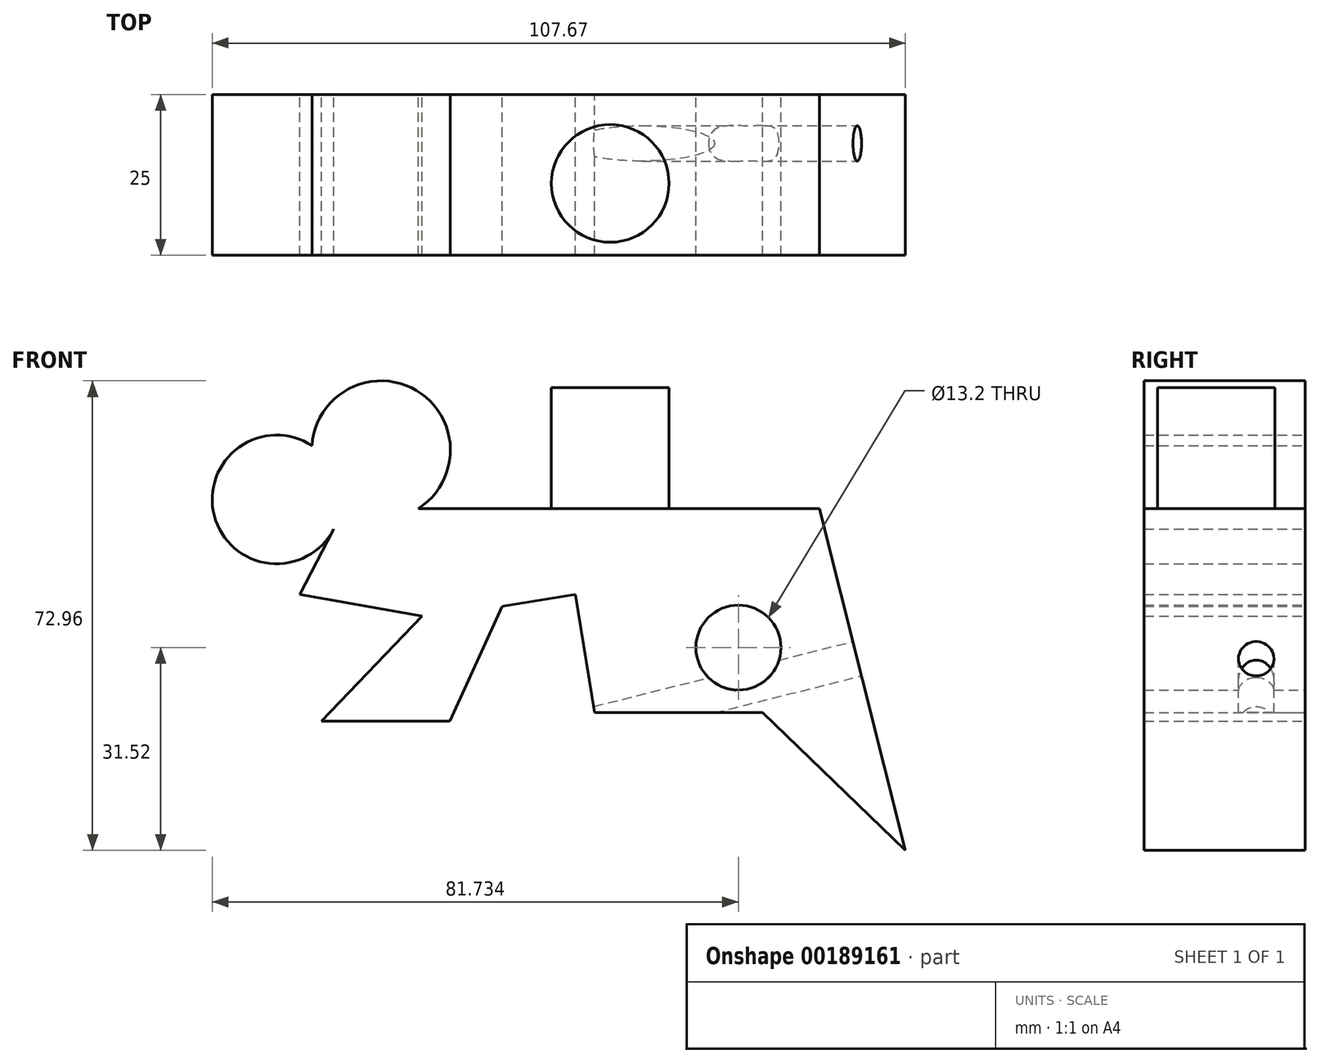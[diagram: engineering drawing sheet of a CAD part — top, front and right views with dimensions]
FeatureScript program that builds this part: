
annotation { "Feature Type Name" : "Feature", "Feature Type Description" : "" }
export const myFeature = defineFeature(function(context is Context, id is Id, definition is map)
    precondition{}
    {
        {
            var Q0;
            Q0=qCreatedBy(makeId("Front.planeOp"),FACE);
            var sketch = newSketch(context, id + "F0", { "sketchPlane" : qUnion([Q0])});
            skLineSegment(sketch, "E0", {"start": v(-41.86, 41.58) * mm, "end": v(20.46, 41.58) * mm});
            skLineSegment(sketch, "E1", {"start": v(20.46, 41.58) * mm, "end": v(33.8, -11.54) * mm});
            skLineSegment(sketch, "E2", {"start": v(33.8, -11.54) * mm, "end": v(11.64, 9.86) * mm});
            skLineSegment(sketch, "E3", {"start": v(11.64, 9.86) * mm, "end": v(-14.45, 9.86) * mm});
            skLineSegment(sketch, "E4", {"start": v(-14.45, 9.86) * mm, "end": v(-17.46, 28.25) * mm});
            skLineSegment(sketch, "E5", {"start": v(-17.46, 28.25) * mm, "end": v(-28.85, 26.4) * mm});
            skLineSegment(sketch, "E6", {"start": v(-28.85, 26.4) * mm, "end": v(-36.98, 8.54) * mm});
            skLineSegment(sketch, "E7", {"start": v(-36.98, 8.54) * mm, "end": v(-56.88, 8.54) * mm});
            skLineSegment(sketch, "E8", {"start": v(-56.88, 8.54) * mm, "end": v(-41.3, 24.87) * mm});
            skLineSegment(sketch, "E9", {"start": v(-41.3, 24.87) * mm, "end": v(-60.26, 28.25) * mm});
            skLineSegment(sketch, "E10", {"start": v(-60.26, 28.25) * mm, "end": v(-55, 38.39) * mm});
            skArc(sketch, "E11", {"start": v(-58.38, 51.34) * mm, "mid": v(-73.55, 40.47) * mm, "end": v(-55, 38.39) * mm});
            skArc(sketch, "E12", {"start": v(-41.86, 41.58) * mm, "mid": v(-42.17, 59.92) * mm, "end": v(-58.38, 51.34) * mm});
            skSolve(sketch);
        }
        {
            var Q0;
            Q0 = qSketchRegion(id + "F0", true);
            extrude(context, id + "F1", {"entities" : qUnion([Q0]), "depth" : 25 * mm});
        }
        {
            var Q0;
            Q0=makeQuery(id+"F1.opExtrude","SWEPT_FACE",FACE,{"disambiguationData":[OSD([sQuery(id+"F0.wireOp",EDGE,"E0")])]});
            var sketch = newSketch(context, id + "F2", { "sketchPlane" : qUnion([Q0])});
            skCircle(sketch, "E13", {"center": v(-12.05, -13.83) * mm, "radius": 9.14 * mm});
            skSolve(sketch);
        }
        {
            var Q0;
            Q0=makeQuery(id+"F2.imprint","IMPRINT",FACE,{"disambiguationData":[TD([[makeQuery(id+"F2.imprint","IMPRINT",EDGE,{"derivedFrom":sQuery(id+"F2.wireOp",EDGE,"E13")}),1.0]])]});
            extrude(context, id + "F3", {"entities" : qUnion([Q0]), "operationType" : NewBodyOperationType.ADD, "depth" : 18.8 * mm});
        }
        {
            var Q0;
            Q0=makeQuery(id+"F1.opExtrude","SWEPT_FACE",FACE,{"disambiguationData":[OSD([sQuery(id+"F0.wireOp",EDGE,"E1")])]});
            var sketch = newSketch(context, id + "F4", { "sketchPlane" : qUnion([Q0])});
            skCircle(sketch, "E14", {"center": v(-10.5, 14.37) * mm, "radius": 2.78 * mm});
            skSolve(sketch);
        }
        {
            var Q0;
            Q0=makeQuery(id+"F4.imprint","IMPRINT",FACE,{"disambiguationData":[TD([[makeQuery(id+"F4.imprint","IMPRINT",EDGE,{"derivedFrom":sQuery(id+"F4.wireOp",EDGE,"E14")}),-1.0]])]});
            var sketch = newSketch(context, id + "F5", { "sketchPlane" : qUnion([Q0])});
            skLineSegment(sketch, "E15", {"start": v(0, 11.67) * mm, "end": v(-25.24, 10.44) * mm});
            skLineSegment(sketch, "E16", {"start": v(-25.24, 10.44) * mm, "end": v(-12.9, 35.12) * mm});
            skLineSegment(sketch, "E17", {"start": v(-12.9, 35.12) * mm, "end": v(-7.6, 11.3) * mm});
            skLineSegment(sketch, "E18", {"start": v(-7.6, 11.3) * mm, "end": v(0, -10.03) * mm});
            skLineSegment(sketch, "E19", {"start": v(0, -10.03) * mm, "end": v(-25.24, 10.44) * mm});
            skSolve(sketch);
        }
        {
            var Q0;
            Q0=sQuery(id+"F5.wireOp",VERTEX,"E18.start");
            var Q1;
            Q1=makeQuery(id+"F1.opExtrude","SWEPT_BODY",BODY,{"disambiguationData":[OSD([sQuery(id+"F0.wireOp",EDGE,"E0"),sQuery(id+"F0.wireOp",EDGE,"E1"),sQuery(id+"F0.wireOp",EDGE,"E2"),sQuery(id+"F0.wireOp",EDGE,"E3"),sQuery(id+"F0.wireOp",EDGE,"E4"),sQuery(id+"F0.wireOp",EDGE,"E5"),sQuery(id+"F0.wireOp",EDGE,"E6"),sQuery(id+"F0.wireOp",EDGE,"E7"),sQuery(id+"F0.wireOp",EDGE,"E8"),sQuery(id+"F0.wireOp",EDGE,"E9"),sQuery(id+"F0.wireOp",EDGE,"E10"),sQuery(id+"F0.wireOp",EDGE,"E11"),sQuery(id+"F0.wireOp",EDGE,"E12")])]});
            hole(context, id + "F6", {"style" : HoleStyle.SIMPLE, "endStyle" : HoleEndStyle.THROUGH, "holeDiameter" : 5.5 * mm, "locations" : qUnion([Q0]), "scope" : qUnion([Q1]), "isTappedThrough" : true});
        }
        {
            var Q0;
            Q0=makeQuery(id+"F1.opExtrude","CAP_FACE",FACE,{"disambiguationData":[OSD([sQuery(id+"F0.wireOp",EDGE,"E0"),sQuery(id+"F0.wireOp",EDGE,"E1"),sQuery(id+"F0.wireOp",EDGE,"E2"),sQuery(id+"F0.wireOp",EDGE,"E3"),sQuery(id+"F0.wireOp",EDGE,"E4"),sQuery(id+"F0.wireOp",EDGE,"E5"),sQuery(id+"F0.wireOp",EDGE,"E6"),sQuery(id+"F0.wireOp",EDGE,"E7"),sQuery(id+"F0.wireOp",EDGE,"E8"),sQuery(id+"F0.wireOp",EDGE,"E9"),sQuery(id+"F0.wireOp",EDGE,"E10"),sQuery(id+"F0.wireOp",EDGE,"E11"),sQuery(id+"F0.wireOp",EDGE,"E12")])],"isStart":true});
            var sketch = newSketch(context, id + "F7", { "sketchPlane" : qUnion([Q0])});
            skLineSegment(sketch, "E20", {"start": v(-1.53, 41.58) * mm, "end": v(-3.3, 9.86) * mm});
            skLineSegment(sketch, "E21", {"start": v(-24.39, 25.93) * mm, "end": v(16.36, 21.5) * mm});
            skSolve(sketch);
        }
        {
            var Q0;
            {var subQ0=makeQuery(id+"F1.opExtrude","CAP_EDGE",EDGE,{"disambiguationData":[OSD([sQuery(id+"F0.wireOp",EDGE,"E2")])],"isStart":true});Q0=makeQuery(id+"F7.imprint","IMPRINT",FACE,{"disambiguationData":[TD([[makeQuery(id+"F7.imprint","IMPRINT",EDGE,{"derivedFrom":subQ0}),1.0]])]});}
            var sketch = newSketch(context, id + "F8", { "sketchPlane" : qUnion([Q0])});
            skCircle(sketch, "E22", {"center": v(-7.85, 19.98) * mm, "radius": 3.6 * mm});
            skSolve(sketch);
        }
        {
            var Q0;
            Q0=sQuery(id+"F8.wireOp",VERTEX,"E22.center");
            var Q1;
            Q1=makeQuery(id+"F1.opExtrude","SWEPT_BODY",BODY,{"disambiguationData":[OSD([sQuery(id+"F0.wireOp",EDGE,"E0"),sQuery(id+"F0.wireOp",EDGE,"E1"),sQuery(id+"F0.wireOp",EDGE,"E2"),sQuery(id+"F0.wireOp",EDGE,"E3"),sQuery(id+"F0.wireOp",EDGE,"E4"),sQuery(id+"F0.wireOp",EDGE,"E5"),sQuery(id+"F0.wireOp",EDGE,"E6"),sQuery(id+"F0.wireOp",EDGE,"E7"),sQuery(id+"F0.wireOp",EDGE,"E8"),sQuery(id+"F0.wireOp",EDGE,"E9"),sQuery(id+"F0.wireOp",EDGE,"E10"),sQuery(id+"F0.wireOp",EDGE,"E11"),sQuery(id+"F0.wireOp",EDGE,"E12")])]});
            hole(context, id + "F9", {"style" : HoleStyle.SIMPLE, "endStyle" : HoleEndStyle.THROUGH, "standardTappedOrClearance" : lookupTablePath({ "standard" : "ISO", "fit" : "Normal", "size" : "M12", "type" : "Clearance" }), "standardBlindInLast" : lookupTablePath({ "fit" : "Standard", "standard" : "ISO", "size" : "M12", "type" : "Clearance" }), "holeDiameter" : 13.2 * mm, "locations" : qUnion([Q0]), "scope" : qUnion([Q1]), "isTappedThrough" : true});
        }
    });
